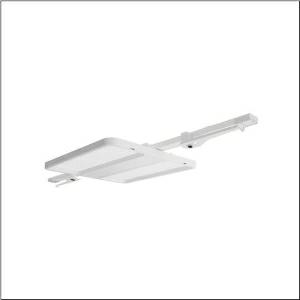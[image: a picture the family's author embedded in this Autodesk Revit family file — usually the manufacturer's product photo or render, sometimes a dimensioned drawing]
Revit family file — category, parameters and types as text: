
# Revit family: highbay_11_fur_modario_r__tragschiene_midi_51hn12da6fma_3b20
name_source: partatom
category: Lighting Fixtures
units: mm (PartAtom-declared; Revit-internal decimal feet)

## family parameters
Cut with Voids When Loaded = No
Host = Face
Light Source = No
Part Type = Normal
Room Calculation Point = No
Round Connector Dimension = Use Diameter
Shared = No

## types (1)
- --- (1 x LED, 14220 lm, 73.2 W, 6500K)
    Apparent Load = 73 VA
    CIE Flux Codes = 87 98 100 100 100
    Color Rendering = 80
    Color Temperature = 6500K
    Default Elevation = 1800 mm
    Description = high bay luminaire Highbay 11 for Modario® trunking rail midi; direct symmetric wide distribution, light control with lens of PMMA; UGR ≤ 22 (X = 4H | Y = 8H | S = 0.25H | reflection values 70/50/20); luminous flux: 14.220lm; light colour: 865, colour temperature: 6500K, MacAdam ≤ 2 SDCM (initial), colour rendering: CRI > 80; luminous efficacy: 194,3lm/W; rated service life: 100.000h (L95/B50) at AT= 25°C; control: DALI 2; luminaire connection: plug, 5-pole, with phase selectionmains connection: 230..240V, AC 50/60Hz; connected load: 73,2W; protection rating (complete): IP64; insulation class (complete): insulation class I (protective earthing); protection symbol: D; impact resistance: IK07; certification: CE, ENEC, VDE, UKCA; internal wiring halogen-free; luminaire corresponds to IFS (International Featured Standards) requirements for safety and quality in the food industry; LABS conformity tested according to VDMA 24364:2018-05; housing frame of high-performance plastic PA6, matt traffic white (RAL 9016); cover of PMMA; fixing on rail side of steel, galvanised, white; blank cover of PC, traffic white (RAL 9016); dimension (LxWxH): 1.195 x 442 x 72mm; permissible operating ambient temperature: -40..+55°C (reducing of maximum allowable ambient temperature of 5°C with ceiling mounting); packaging unit: 1 piece
    Height = 72 mm  [stored 0.23622 ft]
    Lamp = 1 x LED
    Lamp Light Flux = 14220 lm
    Lamp Power = 73.2 W
    Lamp count = 1
    Length = 474 mm
    Luminous efficacy = 194 lm/W
    Manufacturer = Siteco
    ModVariant = No
    Model = 51HN12DA6FMA
    Mounting Place = Ceiling
    Mounting Type = Pendant
    Number of Poles = 1
    OnlyDefault = Yes
    Power Factor = 1
    Product Name = Highbay 11 für Modario® Tragschiene midi
    Product group = high bay luminaire
    ProductGroupID = 901
    Protection Class = Protection class I
    Protection Degree = IP 64
    RLX_Detail_Level = 1
    RLX_Emergency_Light_Flux = 0 lm
    RLX_Emergency_Type = 0
    RLX_Emergency_Type_DB = No
    RlxData = <blob elided: 18037 chars, md5=ab931bb2>
    Socket = socket
    Standby Power = 0 W
    System Light Flux = 14220 lm
    System Power = 73 W
    Type Comments = factory setting: luminous flux: 100 % | dim-lin: 254 | 339 mA
    Type Image = l_1363266.jpg
    URL = http://relux.com
    VarID = @adj_007893
    Voltage = 0 V
    Weight = 0.00 kg
    Width = 442 mm

note: [stored X ft] marks values corroborated as IEEE doubles in the binary element streams (Revit-internal decimal feet)

## geometry (parser evidence)
native form markers: Blend x4, Sweep x10
no freeform markers — native parametric forms only
